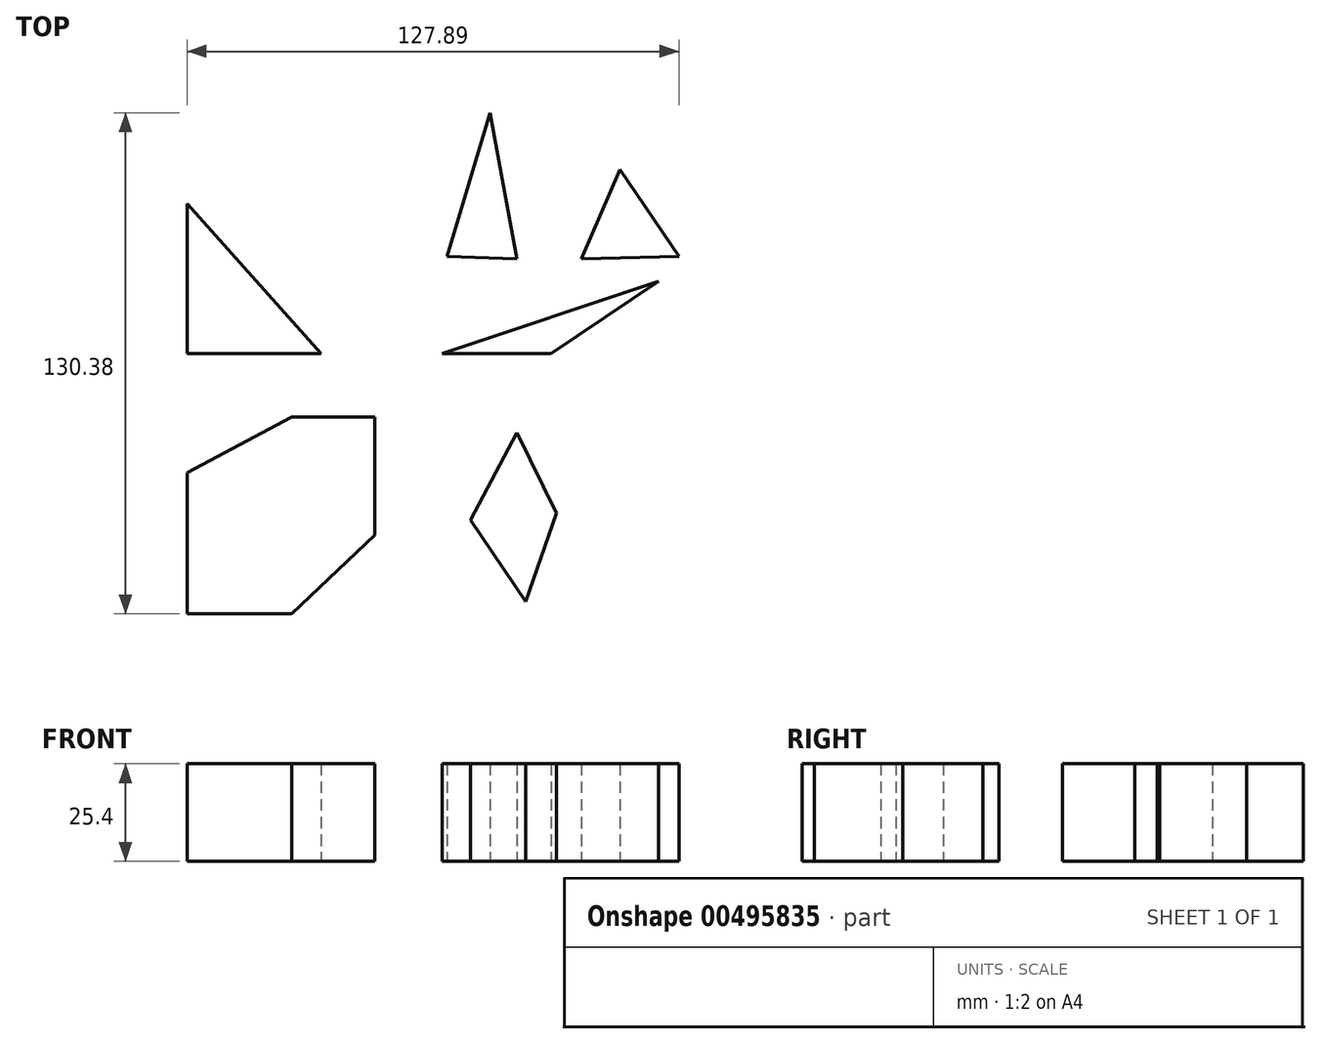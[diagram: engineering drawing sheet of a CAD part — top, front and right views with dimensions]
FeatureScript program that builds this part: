
annotation { "Feature Type Name" : "Feature", "Feature Type Description" : "" }
export const myFeature = defineFeature(function(context is Context, id is Id, definition is map)
    precondition{}
    {
        {
            var Q0;
            Q0=qCreatedBy(makeId("Top.planeOp"),FACE);
            var sketch = newSketch(context, id + "F0", { "sketchPlane" : qUnion([Q0])});
            skLineSegment(sketch, "E0", {"start": v(-58.47, 53.61) * mm, "end": v(-58.47, 14.58) * mm});
            skLineSegment(sketch, "E1", {"start": v(-58.47, 14.58) * mm, "end": v(-23.58, 14.58) * mm});
            skLineSegment(sketch, "E2", {"start": v(-23.58, 14.58) * mm, "end": v(-58.47, 53.61) * mm});
            skLineSegment(sketch, "E3", {"start": v(7.9, 14.58) * mm, "end": v(64.12, 33.42) * mm});
            skLineSegment(sketch, "E4", {"start": v(64.12, 33.42) * mm, "end": v(36.16, 14.58) * mm});
            skLineSegment(sketch, "E5", {"start": v(36.16, 14.58) * mm, "end": v(7.9, 14.58) * mm});
            skLineSegment(sketch, "E6", {"start": v(-58.47, -16.32) * mm, "end": v(-58.47, -53.1) * mm});
            skLineSegment(sketch, "E7", {"start": v(-58.47, -16.32) * mm, "end": v(-31.23, -16.32) * mm});
            skLineSegment(sketch, "E8", {"start": v(-31.23, -16.32) * mm, "end": v(-31.23, -53.1) * mm});
            skLineSegment(sketch, "E9", {"start": v(-58.47, -53.1) * mm, "end": v(-31.23, -53.1) * mm});
            skLineSegment(sketch, "E10", {"start": v(-31.23, -16.32) * mm, "end": v(-9.6, -1.9) * mm});
            skLineSegment(sketch, "E11", {"start": v(-9.6, -1.9) * mm, "end": v(-9.6, -32.68) * mm});
            skLineSegment(sketch, "E12", {"start": v(-31.23, -53.1) * mm, "end": v(-9.6, -32.68) * mm});
            skLineSegment(sketch, "E13", {"start": v(-58.47, -16.32) * mm, "end": v(-31.23, -1.9) * mm});
            skLineSegment(sketch, "E14", {"start": v(-31.23, -1.9) * mm, "end": v(-31.23, -53.1) * mm});
            skLineSegment(sketch, "E15", {"start": v(-31.23, -1.9) * mm, "end": v(-9.6, -1.9) * mm});
            skLineSegment(sketch, "E16", {"start": v(-58.47, -53.1) * mm, "end": v(-31.23, -27.5) * mm});
            skLineSegment(sketch, "E17", {"start": v(-9.6, -32.68) * mm, "end": v(-31.23, -27.5) * mm});
            skLineSegment(sketch, "E18", {"start": v(9.09, 39.9) * mm, "end": v(20.27, 77.27) * mm});
            skLineSegment(sketch, "E19", {"start": v(20.27, 77.27) * mm, "end": v(27.33, 39.3) * mm});
            skLineSegment(sketch, "E20", {"start": v(9.09, 39.9) * mm, "end": v(27.33, 39.3) * mm});
            skLineSegment(sketch, "E21", {"start": v(69.42, 39.9) * mm, "end": v(44.1, 39.3) * mm});
            skLineSegment(sketch, "E22", {"start": v(44.1, 39.3) * mm, "end": v(54.12, 62.56) * mm});
            skLineSegment(sketch, "E23", {"start": v(54.12, 62.56) * mm, "end": v(69.42, 39.9) * mm});
            skLineSegment(sketch, "E24", {"start": v(27.33, -6.02) * mm, "end": v(15.27, -28.68) * mm});
            skLineSegment(sketch, "E25", {"start": v(15.27, -28.68) * mm, "end": v(29.54, -49.87) * mm});
            skLineSegment(sketch, "E26", {"start": v(27.33, -6.02) * mm, "end": v(37.63, -26.91) * mm});
            skLineSegment(sketch, "E27", {"start": v(37.63, -26.91) * mm, "end": v(29.54, -49.87) * mm});
            skLineSegment(sketch, "E28", {"start": v(-97.72, -15.63) * mm, "end": v(-103.72, -26.91) * mm});
            skSolve(sketch);
        }
        {
            var Q0;
            Q0 = qSketchRegion(id + "F0", true);
            extrude(context, id + "F1", {"entities" : qUnion([Q0]), "depth" : 25.4 * mm});
        }
    });
